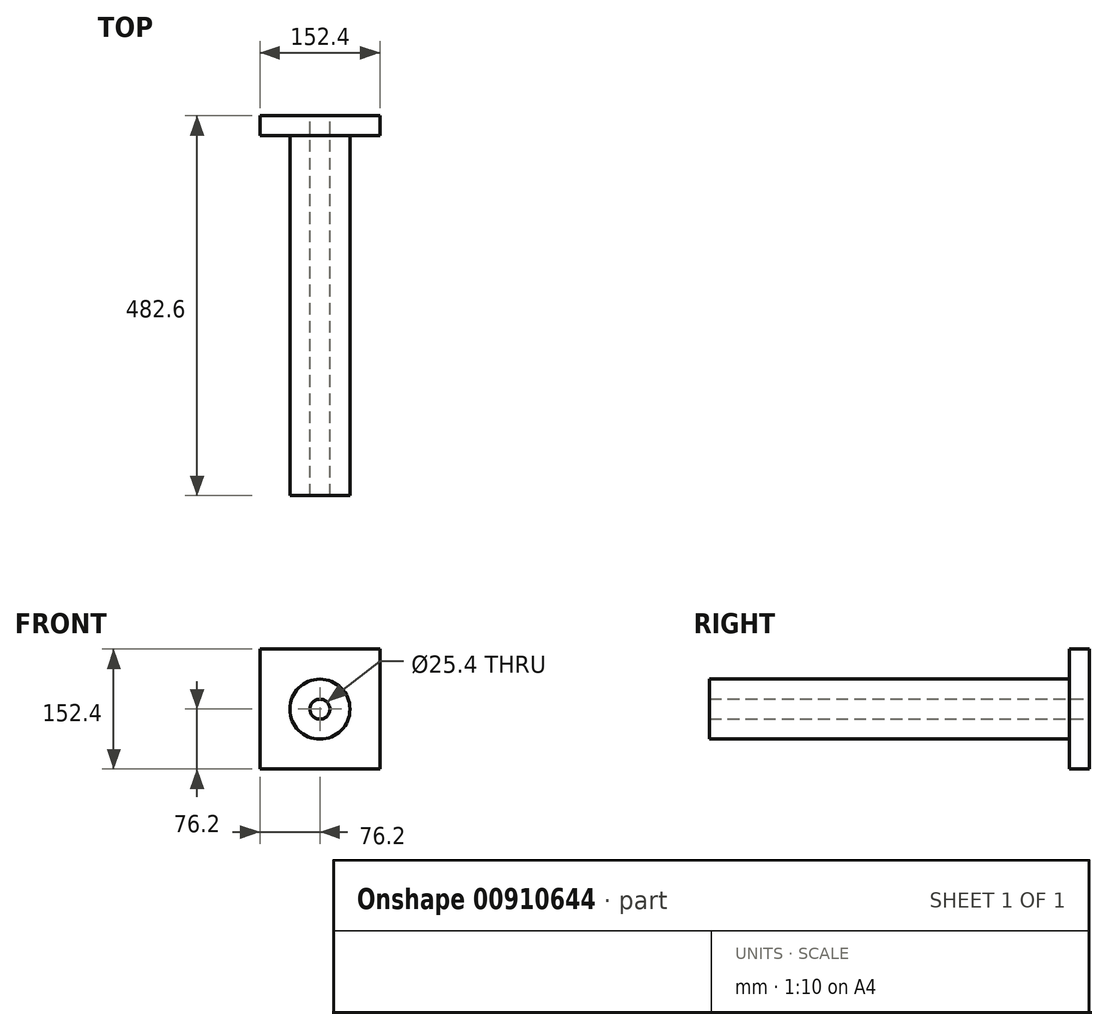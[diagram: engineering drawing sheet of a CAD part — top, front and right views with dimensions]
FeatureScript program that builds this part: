
annotation { "Feature Type Name" : "Feature", "Feature Type Description" : "" }
export const myFeature = defineFeature(function(context is Context, id is Id, definition is map)
    precondition{}
    {
        {
            var Q0;
            Q0=qCreatedBy(makeId("Front.planeOp"),FACE);
            var sketch = newSketch(context, id + "F0", { "sketchPlane" : qUnion([Q0])});
            skLineSegment(sketch, "E0.bottom", {"start": v(0, 0) * mm, "end": v(152.4, 0) * mm});
            skLineSegment(sketch, "E0.top", {"start": v(0, 152.4) * mm, "end": v(152.4, 152.4) * mm});
            skLineSegment(sketch, "E0.left", {"start": v(0, 0) * mm, "end": v(0, 152.4) * mm});
            skLineSegment(sketch, "E0.right", {"start": v(152.4, 0) * mm, "end": v(152.4, 152.4) * mm});
            skSolve(sketch);
        }
        {
            var Q0;
            Q0=makeQuery(id+"F0.imprint","IMPRINT",FACE,{"disambiguationData":[TD([[makeQuery(id+"F0.imprint","IMPRINT",EDGE,{"derivedFrom":sQuery(id+"F0.wireOp",EDGE,"E0.bottom")}),1.0]])]});
            extrude(context, id + "F1", {"entities" : qUnion([Q0]), "depth" : 25.4 * mm, "offsetDistance" : 25.4 * mm});
        }
        {
            var Q0;
            Q0=makeQuery(id+"F1.opExtrude","CAP_FACE",FACE,{"disambiguationData":[OSD([sQuery(id+"F0.wireOp",EDGE,"E0.bottom"),sQuery(id+"F0.wireOp",EDGE,"E0.top"),sQuery(id+"F0.wireOp",EDGE,"E0.left"),sQuery(id+"F0.wireOp",EDGE,"E0.right")])],"isStart":false});
            var sketch = newSketch(context, id + "F2", { "sketchPlane" : qUnion([Q0])});
            skCircle(sketch, "E1", {"center": v(76.2, 76.2) * mm, "radius": 38.1 * mm});
            skLineSegment(sketch, "E2", {"start": v(76.2, 152.4) * mm, "end": v(76.2, 0) * mm, "construction": true});
            skSolve(sketch);
        }
        {
            var Q0;
            Q0 = qSketchRegion(id + "F2", true);
            extrude(context, id + "F3", {"entities" : qUnion([Q0]), "operationType" : NewBodyOperationType.ADD, "depth" : 457.2 * mm, "offsetDistance" : 25.4 * mm});
        }
        {
            var Q0;
            Q0=makeQuery(id+"F1.opExtrude","CAP_FACE",FACE,{"disambiguationData":[OSD([sQuery(id+"F0.wireOp",EDGE,"E0.bottom"),sQuery(id+"F0.wireOp",EDGE,"E0.top"),sQuery(id+"F0.wireOp",EDGE,"E0.left"),sQuery(id+"F0.wireOp",EDGE,"E0.right")])],"isStart":true});
            var sketch = newSketch(context, id + "F4", { "sketchPlane" : qUnion([Q0])});
            skCircle(sketch, "E3", {"center": v(-76.2, 76.2) * mm, "radius": 12.7 * mm});
            skLineSegment(sketch, "E4", {"start": v(-152.4, 76.2) * mm, "end": v(0, 76.2) * mm, "construction": true});
            skSolve(sketch);
        }
        {
            var Q0;
            Q0=makeQuery(id+"F4.imprint","IMPRINT",FACE,{"disambiguationData":[TD([[makeQuery(id+"F4.imprint","IMPRINT",EDGE,{"derivedFrom":sQuery(id+"F4.wireOp",EDGE,"E3")}),1.0]])]});
            extrude(context, id + "F5", {"entities" : qUnion([Q0]), "operationType" : NewBodyOperationType.REMOVE, "endBound" : BoundingType.UP_TO_NEXT, "oppositeDirection" : true, "depth" : 25.4 * mm, "offsetDistance" : 25.4 * mm});
        }
    });
